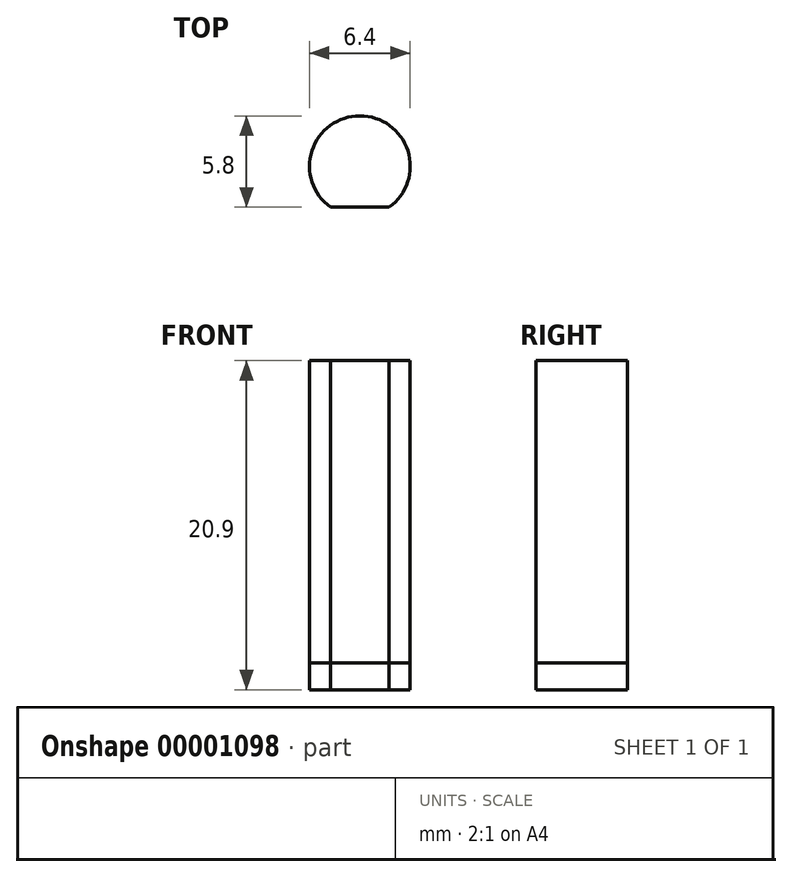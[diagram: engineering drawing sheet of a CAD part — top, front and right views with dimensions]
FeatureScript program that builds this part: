
annotation { "Feature Type Name" : "Feature", "Feature Type Description" : "" }
export const myFeature = defineFeature(function(context is Context, id is Id, definition is map)
    precondition{}
    {
        {
            var Q0;
            Q0=qCreatedBy(makeId("Front.planeOp"),FACE);
            var sketch = newSketch(context, id + "F0", { "sketchPlane" : qUnion([Q0])});
            skLineSegment(sketch, "E0", {"start": v(0, 1.7) * mm, "end": v(19.25, 1.7) * mm});
            skLineSegment(sketch, "E1", {"start": v(19.25, 1.7) * mm, "end": v(19.25, 0) * mm});
            skLineSegment(sketch, "E2", {"start": v(19.25, 0) * mm, "end": v(28.2, 0) * mm});
            skLineSegment(sketch, "E3", {"start": v(28.2, 0) * mm, "end": v(28.2, -14.3) * mm});
            skLineSegment(sketch, "E4", {"start": v(28.2, -14.3) * mm, "end": v(26.75, -14.3) * mm});
            skLineSegment(sketch, "E5", {"start": v(26.75, -14.3) * mm, "end": v(26.75, -58.7) * mm});
            skLineSegment(sketch, "E6", {"start": v(26.75, -58.7) * mm, "end": v(28.2, -58.7) * mm});
            skLineSegment(sketch, "E7", {"start": v(28.2, -58.7) * mm, "end": v(28.2, -76.3) * mm});
            skLineSegment(sketch, "E8", {"start": v(28.2, -76.3) * mm, "end": v(0, -76.3) * mm});
            skLineSegment(sketch, "E9", {"start": v(0, -76.3) * mm, "end": v(0, 20.9) * mm});
            skLineSegment(sketch, "E10", {"start": v(3.2, 1.7) * mm, "end": v(3.2, 20.9) * mm});
            skLineSegment(sketch, "E11", {"start": v(3.2, 20.9) * mm, "end": v(0, 20.9) * mm});
            skSolve(sketch);
        }
        {
            var Q0;
            {var subQ4=sQuery(id+"F0.wireOp",EDGE,"E1");Q0=makeQuery(id+"F0.imprint","IMPRINT",FACE,{"disambiguationData":[TD([[makeQuery(id+"F0.imprint","IMPRINT",EDGE,{"derivedFrom":subQ4}),-1.0]])]});}
            var Q1;
            Q1=sQuery(id+"F0.wireOp",EDGE,"E9");
            revolve(context, id + "F1", {"entities" : qUnion([Q0]), "axis" : qUnion([Q1]), "revolveType" : RevolveType.FULL});
        }
        {
            var Q0;
            Q0=qCreatedBy(makeId("Top.planeOp"),FACE);
            var sketch = newSketch(context, id + "F2", { "sketchPlane" : qUnion([Q0])});
            skLineSegment(sketch, "E12.bottom", {"start": v(28.2, 28.2) * mm, "end": v(-28.2, 28.2) * mm});
            skLineSegment(sketch, "E12.top", {"start": v(28.2, -28.2) * mm, "end": v(-28.2, -28.2) * mm});
            skLineSegment(sketch, "E12.left", {"start": v(28.2, 28.2) * mm, "end": v(28.2, -28.2) * mm});
            skLineSegment(sketch, "E12.right", {"start": v(-28.2, 28.2) * mm, "end": v(-28.2, -28.2) * mm});
            skPoint(sketch, "E12.middle", {"position": v(0, 0) * mm});
            skLineSegment(sketch, "E13.bottom", {"start": v(-23.5, 23.5) * mm, "end": v(23.5, 23.5) * mm, "construction": true});
            skLineSegment(sketch, "E13.top", {"start": v(-23.5, -23.5) * mm, "end": v(23.5, -23.5) * mm, "construction": true});
            skLineSegment(sketch, "E13.left", {"start": v(-23.5, 23.5) * mm, "end": v(-23.5, -23.5) * mm, "construction": true});
            skLineSegment(sketch, "E13.right", {"start": v(23.5, 23.5) * mm, "end": v(23.5, -23.5) * mm, "construction": true});
            skSolve(sketch);
        }
        {
            var Q0;
            Q0=makeQuery(id+"F2.imprint","IMPRINT",FACE,{"disambiguationData":[TD([[makeQuery(id+"F2.imprint","IMPRINT",EDGE,{"derivedFrom":sQuery(id+"F2.wireOp",EDGE,"E12.bottom")}),1.0]])]});
            extrude(context, id + "F3", {"entities" : qUnion([Q0]), "operationType" : NewBodyOperationType.ADD, "oppositeDirection" : true, "depth" : 5 * mm});
        }
        {
            var Q0;
            Q0=makeQuery(id+"F3.opExtrude","SWEPT_EDGE",EDGE,{"disambiguationData":[OSD([sQuery(id+"F2.wireOp",EDGE,"E12.top"),sQuery(id+"F2.wireOp",EDGE,"E12.left")])]});
            var Q1;
            Q1=makeQuery(id+"F3.opExtrude","SWEPT_EDGE",EDGE,{"disambiguationData":[OSD([sQuery(id+"F2.wireOp",EDGE,"E12.top"),sQuery(id+"F2.wireOp",EDGE,"E12.right")])]});
            var Q2;
            Q2=makeQuery(id+"F3.opExtrude","SWEPT_EDGE",EDGE,{"disambiguationData":[OSD([sQuery(id+"F2.wireOp",EDGE,"E12.bottom"),sQuery(id+"F2.wireOp",EDGE,"E12.right")])]});
            var Q3;
            Q3=makeQuery(id+"F3.opExtrude","SWEPT_EDGE",EDGE,{"disambiguationData":[OSD([sQuery(id+"F2.wireOp",EDGE,"E12.bottom"),sQuery(id+"F2.wireOp",EDGE,"E12.left")])]});
            fillet(context, id + "F4", {"entities" : qUnion([Q0, Q1, Q2, Q3]), "radius" : 5 * mm, "tangentPropagation" : true, "allowEdgeOverflow" : false});
        }
        {
            var Q0;
            Q0=sQuery(id+"F2.wireOp",VERTEX,"E13.top.start");
            var Q1;
            Q1=sQuery(id+"F2.wireOp",VERTEX,"E13.left.start");
            var Q2;
            Q2=sQuery(id+"F2.wireOp",VERTEX,"E13.right.start");
            var Q3;
            Q3=sQuery(id+"F2.wireOp",VERTEX,"E13.right.end");
            var Q4;
            Q4=makeQuery(id+"F1.opRevolve","SWEPT_BODY",BODY,{"disambiguationData":[OSD([sQuery(id+"F0.wireOp",EDGE,"E0"),sQuery(id+"F0.wireOp",EDGE,"E1"),sQuery(id+"F0.wireOp",EDGE,"E2"),sQuery(id+"F0.wireOp",EDGE,"E3"),sQuery(id+"F0.wireOp",EDGE,"E4"),sQuery(id+"F0.wireOp",EDGE,"E5"),sQuery(id+"F0.wireOp",EDGE,"E6"),sQuery(id+"F0.wireOp",EDGE,"E7"),sQuery(id+"F0.wireOp",EDGE,"E8"),sQuery(id+"F0.wireOp",EDGE,"E9")])]});
            hole(context, id + "F5", {"style" : HoleStyle.SIMPLE, "endStyle" : HoleEndStyle.THROUGH, "holeDiameter" : 4.5 * mm, "locations" : qUnion([Q0, Q1, Q2, Q3]), "scope" : qUnion([Q4]), "isTappedThrough" : true});
        }
        {
            var Q0;
            {var subQ3=sQuery(id+"F0.wireOp",EDGE,"E10");Q0=makeQuery(id+"F0.imprint","IMPRINT",FACE,{"disambiguationData":[TD([[makeQuery(id+"F0.imprint","IMPRINT",EDGE,{"derivedFrom":subQ3}),1.0]])]});}
            var Q1;
            Q1=sQuery(id+"F0.wireOp",EDGE,"E9");
            revolve(context, id + "F6", {"entities" : qUnion([Q0]), "axis" : qUnion([Q1]), "revolveType" : RevolveType.FULL});
        }
        {
            var Q0;
            Q0=qCreatedBy(makeId("Top.planeOp"),FACE);
            var sketch = newSketch(context, id + "F7", { "sketchPlane" : qUnion([Q0])});
            skLineSegment(sketch, "E14", {"start": v(1.87, -2.6) * mm, "end": v(-1.87, -2.6) * mm});
            skCircle(sketch, "E15", {"center": v(0, 0) * mm, "radius": 3.2 * mm});
            skSolve(sketch);
        }
        {
            var Q0;
            {var subQ0=sQuery(id+"F7.wireOp",EDGE,"E14");Q0=makeQuery(id+"F7.imprint","IMPRINT",FACE,{"disambiguationData":[TD([[makeQuery(id+"F7.imprint","IMPRINT",EDGE,{"derivedFrom":subQ0}),-1.0]])]});}
            extrude(context, id + "F8", {"entities" : qUnion([Q0]), "operationType" : NewBodyOperationType.INTERSECT, "endBound" : BoundingType.THROUGH_ALL, "depth" : 25 * mm});
        }
    });
